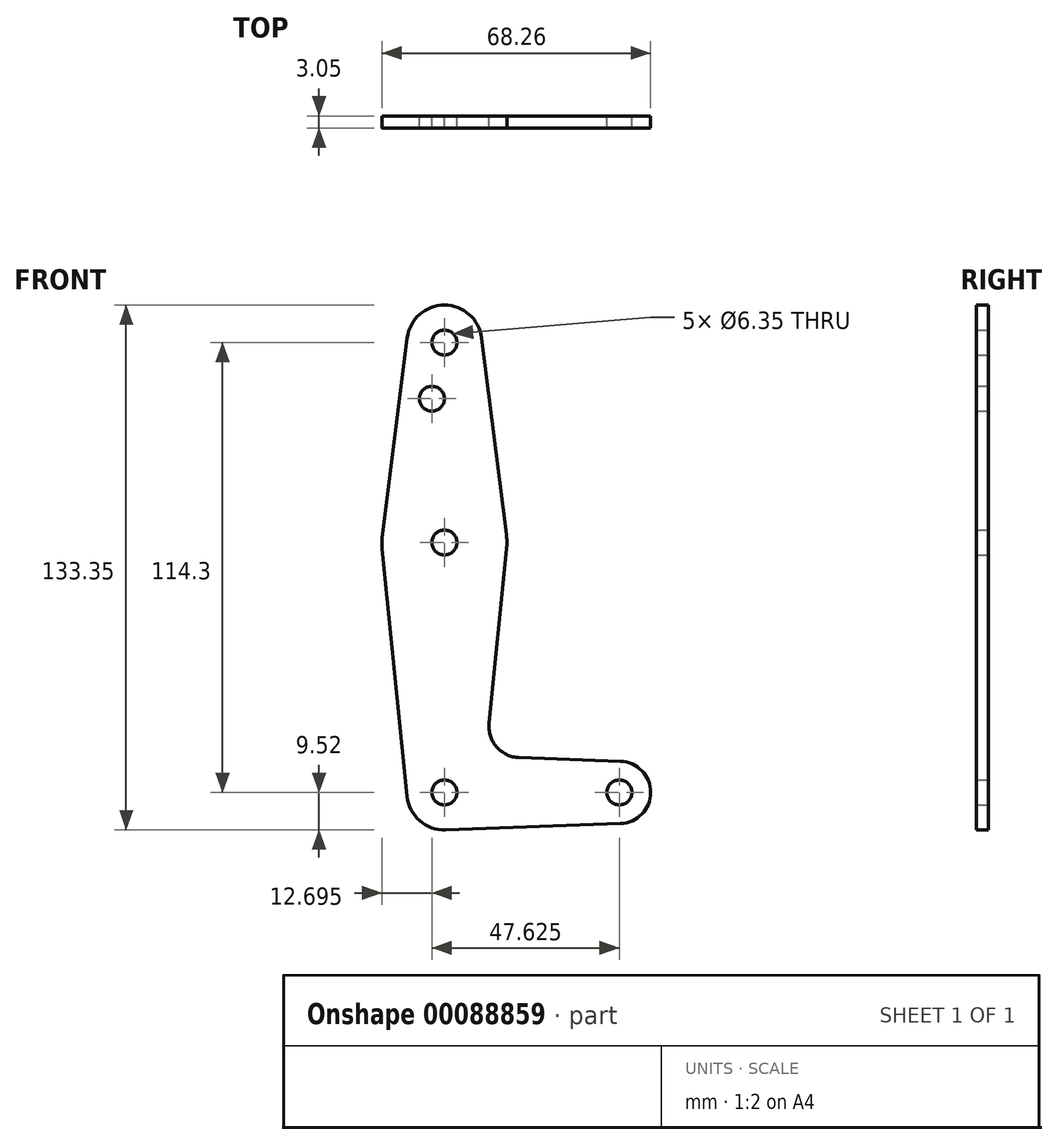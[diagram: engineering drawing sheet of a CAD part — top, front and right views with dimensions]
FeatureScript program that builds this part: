
annotation { "Feature Type Name" : "Feature", "Feature Type Description" : "" }
export const myFeature = defineFeature(function(context is Context, id is Id, definition is map)
    precondition{}
    {
        {
            var Q0;
            Q0=qCreatedBy(makeId("Front.planeOp"),FACE);
            var sketch = newSketch(context, id + "F0", { "sketchPlane" : qUnion([Q0])});
            skLineSegment(sketch, "E0", {"start": v(0, 0) * mm, "end": v(44.45, 0) * mm, "construction": true});
            skCircle(sketch, "E1", {"center": v(0, 114.3) * mm, "radius": 9.53 * mm});
            skCircle(sketch, "E2", {"center": v(0, 0) * mm, "radius": 9.53 * mm});
            skCircle(sketch, "E3", {"center": v(44.45, 0) * mm, "radius": 7.94 * mm});
            skLineSegment(sketch, "E4", {"start": v(0, 114.3) * mm, "end": v(0, 0) * mm, "construction": true});
            skCircle(sketch, "E5", {"center": v(0, 63.5) * mm, "radius": 15.88 * mm});
            skLineSegment(sketch, "E6", {"start": v(44.73, -7.93) * mm, "end": v(0, -9.53) * mm});
            skLineSegment(sketch, "E7", {"start": v(-9.48, -0.95) * mm, "end": v(-15.8, 61.91) * mm});
            skLineSegment(sketch, "E8", {"start": v(11.34, 17.6) * mm, "end": v(15.8, 61.91) * mm});
            skCircle(sketch, "E9", {"center": v(0, 114.3) * mm, "radius": 3.18 * mm});
            skCircle(sketch, "E10", {"center": v(0, 63.5) * mm, "radius": 3.18 * mm});
            skCircle(sketch, "E11", {"center": v(0, 0) * mm, "radius": 3.18 * mm});
            skCircle(sketch, "E12", {"center": v(44.45, 0) * mm, "radius": 3.18 * mm});
            skCircle(sketch, "E13", {"center": v(-3.18, 100.03) * mm, "radius": 3.18 * mm});
            skLineSegment(sketch, "E14", {"start": v(18.97, 8.85) * mm, "end": v(44.73, 7.93) * mm});
            skArc(sketch, "E15.filletArc", {"start": v(11.34, 17.6) * mm, "mid": v(13.26, 11.57) * mm, "end": v(18.97, 8.85) * mm});
            skLineSegment(sketch, "E16", {"start": v(9.45, 115.5) * mm, "end": v(15.75, 65.48) * mm});
            skLineSegment(sketch, "E17", {"start": v(-9.45, 115.5) * mm, "end": v(-15.75, 65.48) * mm});
            skSolve(sketch);
        }
        {
            var Q0;
            Q0 = qSketchRegion(id + "F0", true);
            extrude(context, id + "F1", {"entities" : qUnion([Q0]), "depth" : 3.05 * mm});
        }
    });
